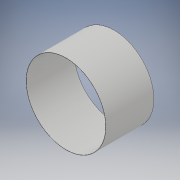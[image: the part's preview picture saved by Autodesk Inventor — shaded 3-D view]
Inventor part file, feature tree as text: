
AUTODESK INVENTOR PART (.ipt)
format: ipt  version: 2019 (Build 230136000, 136)  size: 103,936 bytes
history: native  units: mm
features: extrude x2, sketch x2
ambient origin geometry x8: Origin, YZ Plane, XZ Plane, XY Plane, X Axis, Y Axis, Z Axis, Center Point
bodies: Solid1 (feature_tree)
feature tree (4):
  extrude  "Extrusion1"  Depth=120.2mm TaperAngle=0.0deg
  extrude  "Extrusion2"  Depth=12.02mm TaperAngle=0.0deg
  sketch  "Sketch1"  dims[d0=199.7mm d1=120.2mm d2=0.0mm]
  sketch  "Sketch2"  dims[d3=198.7mm d4=12.02mm d5=0.0mm]
